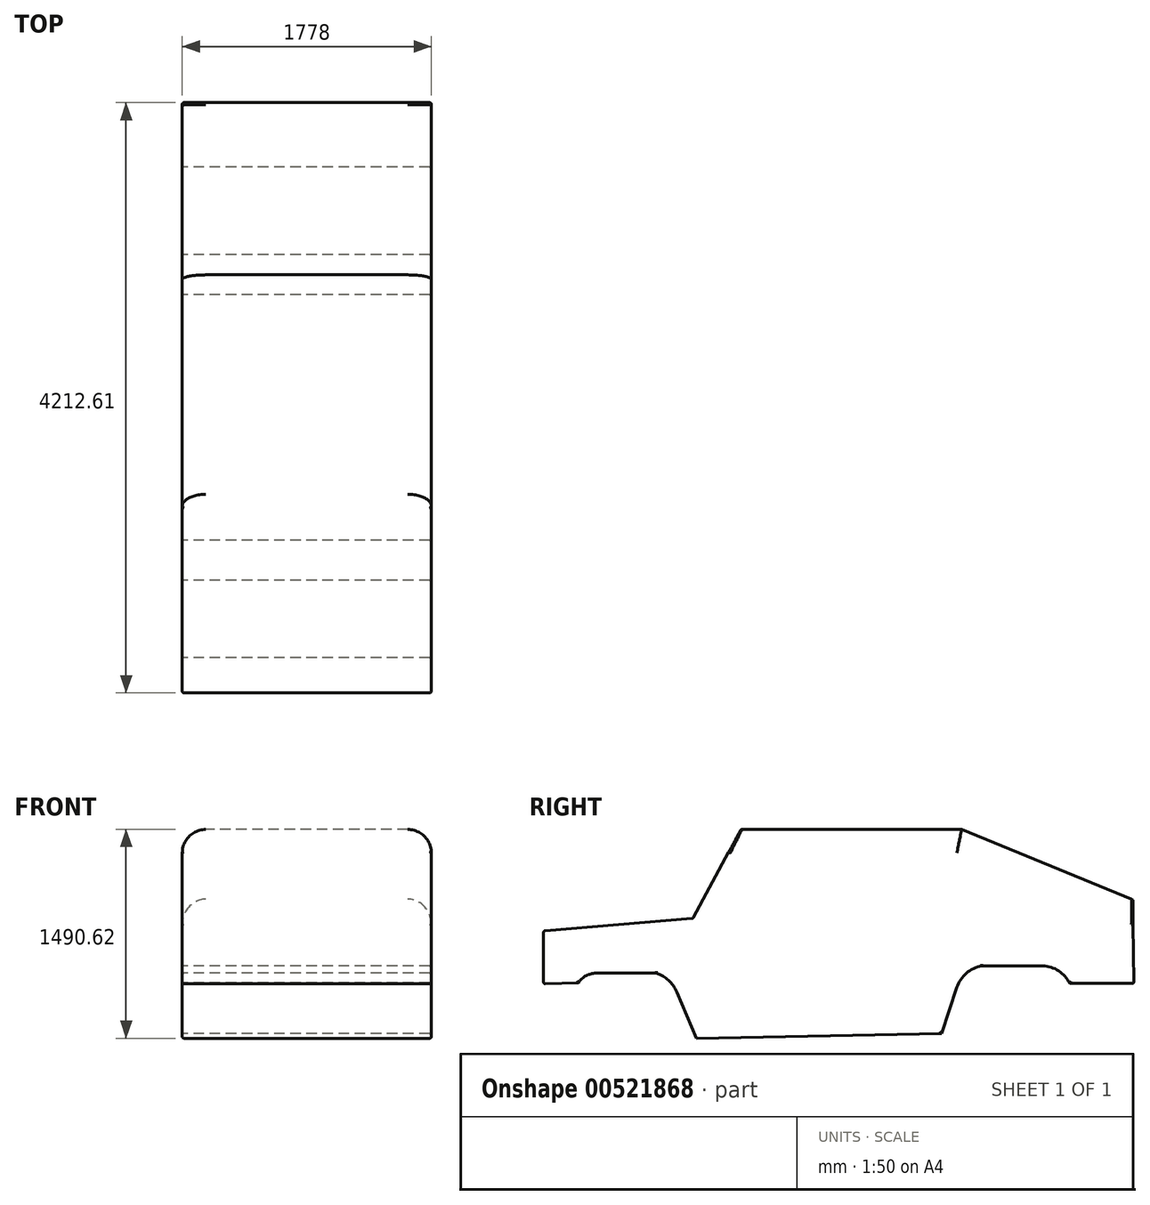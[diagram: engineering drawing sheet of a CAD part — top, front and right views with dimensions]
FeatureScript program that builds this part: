
annotation { "Feature Type Name" : "Feature", "Feature Type Description" : "" }
export const myFeature = defineFeature(function(context is Context, id is Id, definition is map)
    precondition{}
    {
        {
            var Q0;
            Q0=qCreatedBy(makeId("Right.planeOp"),FACE);
            var sketch = newSketch(context, id + "F0", { "sketchPlane" : qUnion([Q0])});
            skLineSegment(sketch, "E0", {"start": v(-667, 564.16) * mm, "end": v(-324.43, 1199.2) * mm});
            skLineSegment(sketch, "E1", {"start": v(1249.81, 1199.28) * mm, "end": v(2472.08, 698.7) * mm});
            skLineSegment(sketch, "E2", {"start": v(2020.41, 99.56) * mm, "end": v(2479.5, 99.56) * mm});
            skLineSegment(sketch, "E3", {"start": v(2472.08, 698.7) * mm, "end": v(2479.5, 99.56) * mm});
            skLineSegment(sketch, "E4", {"start": v(-324.43, 1199.2) * mm, "end": v(1249.81, 1199.28) * mm});
            skLineSegment(sketch, "E5", {"start": v(-1733.26, 474.66) * mm, "end": v(-667, 564.16) * mm});
            skLineSegment(sketch, "E6", {"start": v(-1733.26, 474.66) * mm, "end": v(-1733.26, 97.14) * mm});
            skPoint(sketch, "E6.endSnap0", {"position": v(-1734.14, 97.14) * mm});
            skLineSegment(sketch, "E7", {"start": v(-643.53, -291.34) * mm, "end": v(-782.48, 38.86) * mm});
            skArc(sketch, "E8", {"start": v(-782.48, 38.86) * mm, "mid": v(-840.81, 121.91) * mm, "end": v(-928.34, 173.28) * mm});
            skLineSegment(sketch, "E9", {"start": v(-928.34, 173.28) * mm, "end": v(-1358.81, 173.28) * mm});
            skArc(sketch, "E10", {"start": v(-1358.81, 173.28) * mm, "mid": v(-1429.98, 155.1) * mm, "end": v(-1483.72, 105.03) * mm});
            skLineSegment(sketch, "E11", {"start": v(-1733.26, 97.14) * mm, "end": v(-1483.72, 105.03) * mm});
            skLineSegment(sketch, "E12", {"start": v(1108.08, -258.65) * mm, "end": v(1216.77, 71.55) * mm});
            skArc(sketch, "E13", {"start": v(1216.77, 71.55) * mm, "mid": v(1284.3, 172.72) * mm, "end": v(1394.3, 224.63) * mm});
            skLineSegment(sketch, "E14", {"start": v(1394.3, 224.63) * mm, "end": v(1827.79, 223.96) * mm});
            skPoint(sketch, "E14.endSnap0", {"position": v(1571.8, 223.96) * mm});
            skArc(sketch, "E15", {"start": v(1827.79, 223.96) * mm, "mid": v(1942.39, 190.07) * mm, "end": v(2020.41, 99.56) * mm});
            skLineSegment(sketch, "E16", {"start": v(-643.53, -291.34) * mm, "end": v(1108.08, -258.65) * mm});
            skLineSegment(sketch, "E17", {"start": v(-414.86, 1031.57) * mm, "end": v(1248.55, 1031.57) * mm});
            skLineSegment(sketch, "E18", {"start": v(1248.55, 1031.57) * mm, "end": v(1374.5, 530.05) * mm});
            skLineSegment(sketch, "E19", {"start": v(2443.56, 530.05) * mm, "end": v(1374.5, 530.05) * mm});
            skLineSegment(sketch, "E20", {"start": v(2443.56, 530.05) * mm, "end": v(2474.17, 530.05) * mm});
            skSolve(sketch);
        }
        {
            var Q0;
            {var subQ4=sQuery(id+"F0.wireOp",EDGE,"E2");Q0=makeQuery(id+"F0.imprint","IMPRINT",FACE,{"disambiguationData":[TD([[makeQuery(id+"F0.imprint","IMPRINT",EDGE,{"derivedFrom":subQ4}),1.0]])]});}
            extrude(context, id + "F1", {"entities" : qUnion([Q0]), "depth" : 1778 * mm, "offsetDistance" : 25.4 * mm});
        }
        {
            var Q0;
            Q0=makeQuery(id+"F1.opExtrude","CAP_FACE",FACE,{"disambiguationData":[OSD([sQuery(id+"F0.wireOp",EDGE,"E0"),sQuery(id+"F0.wireOp",EDGE,"E2"),sQuery(id+"F0.wireOp",EDGE,"E3"),sQuery(id+"F0.wireOp",EDGE,"E5"),sQuery(id+"F0.wireOp",EDGE,"E6"),sQuery(id+"F0.wireOp",EDGE,"E7"),sQuery(id+"F0.wireOp",EDGE,"E8"),sQuery(id+"F0.wireOp",EDGE,"E9"),sQuery(id+"F0.wireOp",EDGE,"E10"),sQuery(id+"F0.wireOp",EDGE,"E11"),sQuery(id+"F0.wireOp",EDGE,"E12"),sQuery(id+"F0.wireOp",EDGE,"E13"),sQuery(id+"F0.wireOp",EDGE,"E14"),sQuery(id+"F0.wireOp",EDGE,"E15"),sQuery(id+"F0.wireOp",EDGE,"E16"),sQuery(id+"F0.wireOp",EDGE,"E17"),sQuery(id+"F0.wireOp",EDGE,"E18"),sQuery(id+"F0.wireOp",EDGE,"E19"),sQuery(id+"F0.wireOp",EDGE,"E20")])],"isStart":false});
            var Q1;
            Q1=makeQuery(id+"F1.opExtrude","SWEPT_BODY",BODY,{"disambiguationData":[OSD([sQuery(id+"F0.wireOp",EDGE,"E0"),sQuery(id+"F0.wireOp",EDGE,"E2"),sQuery(id+"F0.wireOp",EDGE,"E3"),sQuery(id+"F0.wireOp",EDGE,"E5"),sQuery(id+"F0.wireOp",EDGE,"E6"),sQuery(id+"F0.wireOp",EDGE,"E7"),sQuery(id+"F0.wireOp",EDGE,"E8"),sQuery(id+"F0.wireOp",EDGE,"E9"),sQuery(id+"F0.wireOp",EDGE,"E10"),sQuery(id+"F0.wireOp",EDGE,"E11"),sQuery(id+"F0.wireOp",EDGE,"E12"),sQuery(id+"F0.wireOp",EDGE,"E13"),sQuery(id+"F0.wireOp",EDGE,"E14"),sQuery(id+"F0.wireOp",EDGE,"E15"),sQuery(id+"F0.wireOp",EDGE,"E16"),sQuery(id+"F0.wireOp",EDGE,"E17"),sQuery(id+"F0.wireOp",EDGE,"E18"),sQuery(id+"F0.wireOp",EDGE,"E19"),sQuery(id+"F0.wireOp",EDGE,"E20")])]});
            shell(context, id + "F2", {"isHollow" : true, "entities" : qUnion([Q0]), "parts" : qUnion([Q1]), "thickness" : 15.88 * mm});
        }
        {
            var Q0;
            Q0 = qSketchRegion(id + "F0", true);
            extrude(context, id + "F3", {"entities" : qUnion([Q0]), "operationType" : NewBodyOperationType.ADD, "depth" : 1778 * mm, "offsetDistance" : 25.4 * mm});
        }
        {
            var Q0;
            Q0=makeQuery(id+"F3.opExtrude","CAP_EDGE",EDGE,{"disambiguationData":[OSD([sQuery(id+"F0.wireOp",EDGE,"E4")])],"isStart":false});
            var Q1;
            Q1=makeQuery(id+"F3.opExtrude","CAP_EDGE",EDGE,{"disambiguationData":[OSD([sQuery(id+"F0.wireOp",EDGE,"E4")])],"isStart":true});
            var Q2;
            Q2=makeQuery(id+"F3.opExtrude","CAP_EDGE",EDGE,{"disambiguationData":[OSD([sQuery(id+"F0.wireOp",EDGE,"E1")])],"isStart":false});
            var Q3;
            Q3=makeQuery(id+"F3.opExtrude","CAP_EDGE",EDGE,{"disambiguationData":[OSD([sQuery(id+"F0.wireOp",EDGE,"E1")])],"isStart":true});
            fillet(context, id + "F4", {"entities" : qUnion([Q0, Q1, Q2, Q3]), "radius" : 168.4 * mm, "tangentPropagation" : true, "allowEdgeOverflow" : false});
        }
        {
            var Q0;
            {var subQ0=sQuery(id+"F0.wireOp",EDGE,"E0");Q0=makeQuery(id+"F3.boolean.opBoolean","MERGE",EDGE,{"derivedFrom":[makeQuery(id+"F1.opExtrude","CAP_EDGE",EDGE,{"disambiguationData":[OSD([subQ0])],"isStart":true}),makeQuery(id+"F3.opExtrude","CAP_EDGE",EDGE,{"disambiguationData":[OSD([subQ0])],"isStart":true})]});}
            var Q1;
            {var subQ0=sQuery(id+"F0.wireOp",EDGE,"E0");Q1=makeQuery(id+"F4.opFillet","BLEND_EDGE",EDGE,{"blendedFrom":[makeQuery(id+"F3.opExtrude","CAP_EDGE",EDGE,{"disambiguationData":[OSD([sQuery(id+"F0.wireOp",EDGE,"E4")])],"isStart":true}),makeQuery(id+"F3.boolean.opBoolean","MERGE",FACE,{"derivedFrom":[makeQuery(id+"F1.opExtrude","SWEPT_FACE",FACE,{"disambiguationData":[OSD([subQ0])]}),makeQuery(id+"F3.opExtrude","SWEPT_FACE",FACE,{"disambiguationData":[OSD([subQ0])]})]})],"blendedInto":[makeQuery(id+"F3.boolean.opBoolean","MERGE",FACE,{"derivedFrom":[makeQuery(id+"F1.opExtrude","SWEPT_FACE",FACE,{"disambiguationData":[OSD([subQ0])]}),makeQuery(id+"F3.opExtrude","SWEPT_FACE",FACE,{"disambiguationData":[OSD([subQ0])]})]})]});}
            var Q2;
            Q2=makeQuery(id+"F3.opExtrude","SWEPT_EDGE",EDGE,{"disambiguationData":[OSD([sQuery(id+"F0.wireOp",EDGE,"E0"),sQuery(id+"F0.wireOp",EDGE,"E4")])]});
            var Q3;
            {var subQ0=sQuery(id+"F0.wireOp",EDGE,"E0");Q3=makeQuery(id+"F4.opFillet","BLEND_EDGE",EDGE,{"blendedFrom":[makeQuery(id+"F3.opExtrude","CAP_EDGE",EDGE,{"disambiguationData":[OSD([sQuery(id+"F0.wireOp",EDGE,"E4")])],"isStart":false}),makeQuery(id+"F3.boolean.opBoolean","MERGE",FACE,{"derivedFrom":[makeQuery(id+"F1.opExtrude","SWEPT_FACE",FACE,{"disambiguationData":[OSD([subQ0])]}),makeQuery(id+"F3.opExtrude","SWEPT_FACE",FACE,{"disambiguationData":[OSD([subQ0])]})]})],"blendedInto":[makeQuery(id+"F3.boolean.opBoolean","MERGE",FACE,{"derivedFrom":[makeQuery(id+"F1.opExtrude","SWEPT_FACE",FACE,{"disambiguationData":[OSD([subQ0])]}),makeQuery(id+"F3.opExtrude","SWEPT_FACE",FACE,{"disambiguationData":[OSD([subQ0])]})]})]});}
            var Q4;
            {var subQ0=sQuery(id+"F0.wireOp",EDGE,"E0");Q4=makeQuery(id+"F3.boolean.opBoolean","MERGE",FACE,{"derivedFrom":[makeQuery(id+"F1.opExtrude","SWEPT_FACE",FACE,{"disambiguationData":[OSD([subQ0])]}),makeQuery(id+"F3.opExtrude","SWEPT_FACE",FACE,{"disambiguationData":[OSD([subQ0])]})]});}
            var Q5;
            Q5=makeQuery(id+"F1.opExtrude","SWEPT_EDGE",EDGE,{"disambiguationData":[OSD([sQuery(id+"F0.wireOp",EDGE,"E5"),sQuery(id+"F0.wireOp",EDGE,"E6")])]});
            var Q6;
            Q6=makeQuery(id+"F1.opExtrude","CAP_EDGE",EDGE,{"disambiguationData":[OSD([sQuery(id+"F0.wireOp",EDGE,"E6")])],"isStart":false});
            var Q7;
            Q7=makeQuery(id+"F1.opExtrude","SWEPT_FACE",FACE,{"disambiguationData":[OSD([sQuery(id+"F0.wireOp",EDGE,"E6")])]});
            var Q8;
            Q8=makeQuery(id+"F1.opExtrude","CAP_EDGE",EDGE,{"disambiguationData":[OSD([sQuery(id+"F0.wireOp",EDGE,"E11")])],"isStart":true});
            var Q9;
            {var subQ0=sQuery(id+"F0.wireOp",EDGE,"E16");var subQ1=sQuery(id+"F0.wireOp",EDGE,"E15");var subQ2=sQuery(id+"F0.wireOp",EDGE,"E14");var subQ3=sQuery(id+"F0.wireOp",EDGE,"E13");var subQ4=sQuery(id+"F0.wireOp",EDGE,"E12");var subQ5=sQuery(id+"F0.wireOp",EDGE,"E11");var subQ6=sQuery(id+"F0.wireOp",EDGE,"E10");var subQ7=sQuery(id+"F0.wireOp",EDGE,"E9");var subQ8=sQuery(id+"F0.wireOp",EDGE,"E8");var subQ9=sQuery(id+"F0.wireOp",EDGE,"E7");var subQ10=sQuery(id+"F0.wireOp",EDGE,"E6");var subQ11=sQuery(id+"F0.wireOp",EDGE,"E5");var subQ12=sQuery(id+"F0.wireOp",EDGE,"E3");var subQ13=sQuery(id+"F0.wireOp",EDGE,"E2");var subQ14=sQuery(id+"F0.wireOp",EDGE,"E0");Q9=makeQuery(id+"F3.boolean.opBoolean","MERGE",FACE,{"derivedFrom":[makeQuery(id+"F1.opExtrude","CAP_FACE",FACE,{"disambiguationData":[OSD([subQ14,subQ13,subQ12,subQ11,subQ10,subQ9,subQ8,subQ7,subQ6,subQ5,subQ4,subQ3,subQ2,subQ1,subQ0,sQuery(id+"F0.wireOp",EDGE,"E17"),sQuery(id+"F0.wireOp",EDGE,"E18"),sQuery(id+"F0.wireOp",EDGE,"E19"),sQuery(id+"F0.wireOp",EDGE,"E20")])],"isStart":true}),makeQuery(id+"F3.opExtrude","CAP_FACE",FACE,{"disambiguationData":[OSD([subQ14,sQuery(id+"F0.wireOp",EDGE,"E1"),subQ13,subQ12,sQuery(id+"F0.wireOp",EDGE,"E4"),subQ11,subQ10,subQ9,subQ8,subQ7,subQ6,subQ5,subQ4,subQ3,subQ2,subQ1,subQ0])],"isStart":true})]});}
            var Q10;
            Q10=makeQuery(id+"F1.opExtrude","CAP_EDGE",EDGE,{"disambiguationData":[OSD([sQuery(id+"F0.wireOp",EDGE,"E11")])],"isStart":false});
            var Q11;
            Q11=makeQuery(id+"F1.opExtrude","CAP_EDGE",EDGE,{"disambiguationData":[OSD([sQuery(id+"F0.wireOp",EDGE,"E10")])],"isStart":false});
            var Q12;
            Q12=makeQuery(id+"F1.opExtrude","CAP_EDGE",EDGE,{"disambiguationData":[OSD([sQuery(id+"F0.wireOp",EDGE,"E8")])],"isStart":false});
            var Q13;
            Q13=makeQuery(id+"F1.opExtrude","CAP_EDGE",EDGE,{"disambiguationData":[OSD([sQuery(id+"F0.wireOp",EDGE,"E16")])],"isStart":false});
            var Q14;
            {var subQ0=sQuery(id+"F0.wireOp",EDGE,"E16");var subQ1=sQuery(id+"F0.wireOp",EDGE,"E15");var subQ2=sQuery(id+"F0.wireOp",EDGE,"E14");var subQ3=sQuery(id+"F0.wireOp",EDGE,"E13");var subQ4=sQuery(id+"F0.wireOp",EDGE,"E12");var subQ5=sQuery(id+"F0.wireOp",EDGE,"E11");var subQ6=sQuery(id+"F0.wireOp",EDGE,"E10");var subQ7=sQuery(id+"F0.wireOp",EDGE,"E9");var subQ8=sQuery(id+"F0.wireOp",EDGE,"E8");var subQ9=sQuery(id+"F0.wireOp",EDGE,"E7");var subQ10=sQuery(id+"F0.wireOp",EDGE,"E6");var subQ11=sQuery(id+"F0.wireOp",EDGE,"E5");var subQ12=sQuery(id+"F0.wireOp",EDGE,"E3");var subQ13=sQuery(id+"F0.wireOp",EDGE,"E2");var subQ14=sQuery(id+"F0.wireOp",EDGE,"E0");Q14=makeQuery(id+"F3.boolean.opBoolean","MERGE",FACE,{"derivedFrom":[makeQuery(id+"F1.opExtrude","CAP_FACE",FACE,{"disambiguationData":[OSD([subQ14,subQ13,subQ12,subQ11,subQ10,subQ9,subQ8,subQ7,subQ6,subQ5,subQ4,subQ3,subQ2,subQ1,subQ0,sQuery(id+"F0.wireOp",EDGE,"E17"),sQuery(id+"F0.wireOp",EDGE,"E18"),sQuery(id+"F0.wireOp",EDGE,"E19"),sQuery(id+"F0.wireOp",EDGE,"E20")])],"isStart":false}),makeQuery(id+"F3.opExtrude","CAP_FACE",FACE,{"disambiguationData":[OSD([subQ14,sQuery(id+"F0.wireOp",EDGE,"E1"),subQ13,subQ12,sQuery(id+"F0.wireOp",EDGE,"E4"),subQ11,subQ10,subQ9,subQ8,subQ7,subQ6,subQ5,subQ4,subQ3,subQ2,subQ1,subQ0])],"isStart":false})]});}
            var Q15;
            Q15=makeQuery(id+"F1.opExtrude","SWEPT_EDGE",EDGE,{"disambiguationData":[OSD([sQuery(id+"F0.wireOp",EDGE,"E2"),sQuery(id+"F0.wireOp",EDGE,"E3")])]});
            fillet(context, id + "F5", {"entities" : qUnion([Q0, Q1, Q2, Q3, Q4, Q5, Q6, Q7, Q8, Q9, Q10, Q11, Q12, Q13, Q14, Q15]), "radius" : 12.7 * mm, "tangentPropagation" : true, "allowEdgeOverflow" : false});
        }
    });
